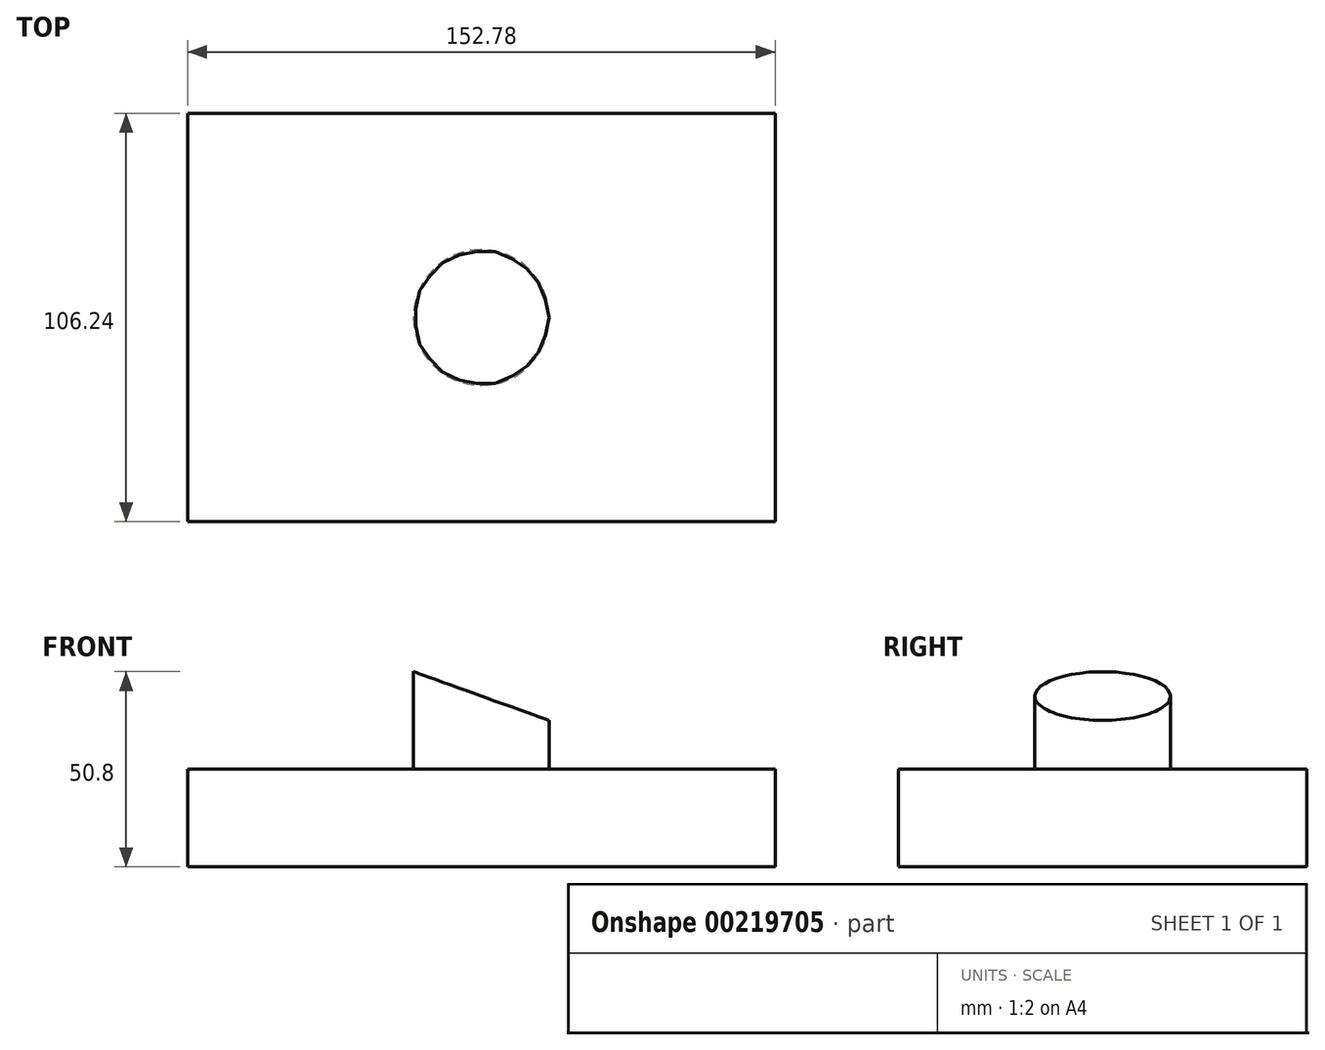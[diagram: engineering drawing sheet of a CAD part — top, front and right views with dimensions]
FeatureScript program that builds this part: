
annotation { "Feature Type Name" : "Feature", "Feature Type Description" : "" }
export const myFeature = defineFeature(function(context is Context, id is Id, definition is map)
    precondition{}
    {
        {
            var Q0;
            Q0=qCreatedBy(makeId("Top.planeOp"),FACE);
            var sketch = newSketch(context, id + "F0", { "sketchPlane" : qUnion([Q0])});
            skLineSegment(sketch, "E0.bottom", {"start": v(-76.4, -53.12) * mm, "end": v(76.4, -53.12) * mm});
            skLineSegment(sketch, "E0.top", {"start": v(-76.4, 53.12) * mm, "end": v(76.4, 53.12) * mm});
            skLineSegment(sketch, "E0.left", {"start": v(-76.4, -53.12) * mm, "end": v(-76.4, 53.12) * mm});
            skLineSegment(sketch, "E0.right", {"start": v(76.4, -53.12) * mm, "end": v(76.4, 53.12) * mm});
            skPoint(sketch, "E0.middle", {"position": v(0, 0) * mm});
            skLineSegment(sketch, "E1.bottom", {"start": v(-76.4, 57.02) * mm, "end": v(-76.4, 57.02) * mm});
            skLineSegment(sketch, "E1.top", {"start": v(-76.4, 49.23) * mm, "end": v(-76.4, 49.23) * mm});
            skLineSegment(sketch, "E1.left", {"start": v(-76.4, 57.02) * mm, "end": v(-76.4, 49.23) * mm});
            skLineSegment(sketch, "E1.right", {"start": v(-76.4, 57.02) * mm, "end": v(-76.4, 49.23) * mm});
            skPoint(sketch, "E1.middle", {"position": v(-76.4, 53.12) * mm});
            skSolve(sketch);
        }
        {
            var Q0;
            Q0=qCreatedBy(makeId("Top.planeOp"),FACE);
            var sketch = newSketch(context, id + "F1", { "sketchPlane" : qUnion([Q0])});
            skCircle(sketch, "E2", {"center": v(0, 0) * mm, "radius": 17.64 * mm});
            skSolve(sketch);
        }
        {
            var Q0;
            Q0=makeQuery(id+"F0.imprint","IMPRINT",FACE,{"disambiguationData":[TD([[makeQuery(id+"F0.imprint","IMPRINT",EDGE,{"derivedFrom":sQuery(id+"F0.wireOp",EDGE,"E0.bottom")}),1.0]])]});
            extrude(context, id + "F2", {"entities" : qUnion([Q0]), "depth" : 25.4 * mm});
        }
        {
            var Q0;
            Q0 = qSketchRegion(id + "F1", true);
            extrude(context, id + "F3", {"entities" : qUnion([Q0]), "operationType" : NewBodyOperationType.ADD, "depth" : 50.8 * mm});
        }
        {
            var Q0;
            Q0=makeQuery(id+"F2.opExtrude","SWEPT_FACE",FACE,{"disambiguationData":[OSD([sQuery(id+"F0.wireOp",EDGE,"E0.bottom")])]});
            var sketch = newSketch(context, id + "F4", { "sketchPlane" : qUnion([Q0])});
            skLineSegment(sketch, "E3.0", {"start": v(-17.64, 50.8) * mm, "end": v(17.64, 50.8) * mm});
            skLineSegment(sketch, "E4", {"start": v(17.64, 50.8) * mm, "end": v(17.64, 25.4) * mm});
            skLineSegment(sketch, "E5", {"start": v(-17.64, 50.8) * mm, "end": v(17.64, 38.1) * mm});
            skSolve(sketch);
        }
        {
            var Q0;
            {var subQ0=sQuery(id+"F4.wireOp",EDGE,"E3.0");Q0=makeQuery(id+"F4.imprint","IMPRINT",FACE,{"disambiguationData":[TD([[makeQuery(id+"F4.imprint","IMPRINT",EDGE,{"derivedFrom":subQ0}),-1.0]])]});}
            extrude(context, id + "F5", {"entities" : qUnion([Q0]), "operationType" : NewBodyOperationType.REMOVE, "endBound" : BoundingType.THROUGH_ALL, "oppositeDirection" : true, "depth" : 25.4 * mm});
        }
    });
